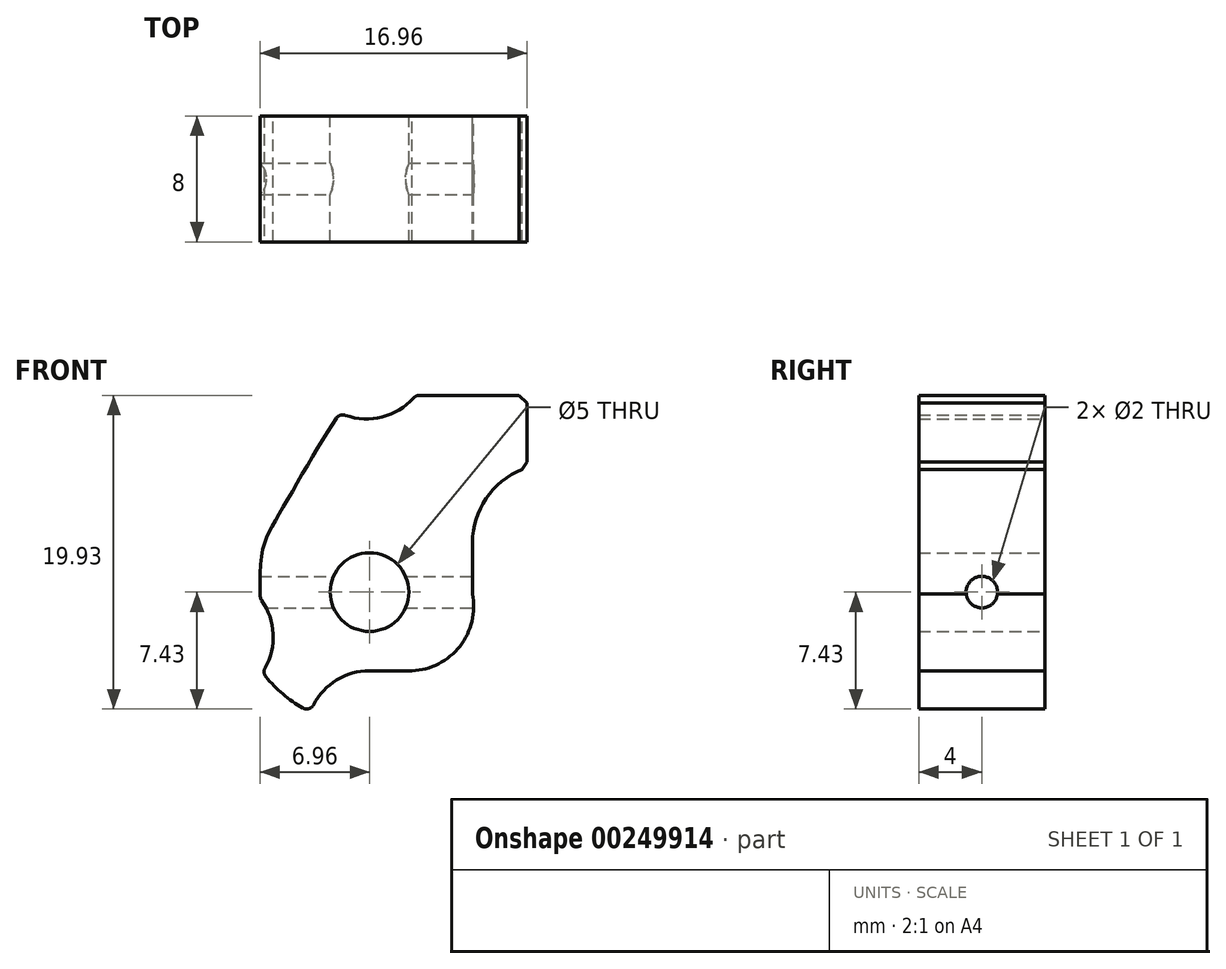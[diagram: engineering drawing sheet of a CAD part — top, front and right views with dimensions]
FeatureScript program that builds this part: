
annotation { "Feature Type Name" : "Feature", "Feature Type Description" : "" }
export const myFeature = defineFeature(function(context is Context, id is Id, definition is map)
    precondition{}
    {
        {
            var Q0;
            Q0=qCreatedBy(makeId("Front.planeOp"),FACE);
            var sketch = newSketch(context, id + "F0", { "sketchPlane" : qUnion([Q0])});
            skCircle(sketch, "E0", {"center": v(0, 0) * mm, "radius": 2.5 * mm});
            skLineSegment(sketch, "E1", {"start": v(0, -5) * mm, "end": v(2.7, -5) * mm});
            skArc(sketch, "E2", {"start": v(0, -5) * mm, "mid": v(-2.3, -5.72) * mm, "end": v(-3.76, -7.63) * mm});
            skArc(sketch, "E3", {"start": v(-6.8, -5.1) * mm, "mid": v(-6.12, -2.74) * mm, "end": v(-6.93, -0.43) * mm});
            skArc(sketch, "E4", {"start": v(-6.8, -5.1) * mm, "mid": v(-5.43, -6.54) * mm, "end": v(-3.76, -7.63) * mm});
            skLineSegment(sketch, "E5", {"start": v(6.54, -0.1) * mm, "end": v(6.54, 3.15) * mm});
            skArc(sketch, "E6.trimOffspring", {"start": v(2.7, -5) * mm, "mid": v(5.74, -3.44) * mm, "end": v(6.54, -0.1) * mm});
            skLineSegment(sketch, "E7", {"start": v(2.94, 12.5) * mm, "end": v(10, 12.5) * mm});
            skLineSegment(sketch, "E8", {"start": v(10, 12.5) * mm, "end": v(10, 7.9) * mm});
            skArc(sketch, "E9", {"start": v(10, 7.9) * mm, "mid": v(7.5, 6.09) * mm, "end": v(6.54, 3.15) * mm});
            skArc(sketch, "E10", {"start": v(-1.87, 11.37) * mm, "mid": v(0.73, 11.1) * mm, "end": v(2.94, 12.5) * mm});
            skPoint(sketch, "E11.orphan", {"position": v(0, 12.5) * mm});
            skPoint(sketch, "E12", {"position": v(-3.3, 12.5) * mm});
            skPoint(sketch, "E13.orphan", {"position": v(12.52, 15) * mm});
            skPoint(sketch, "E14.start.orphan", {"position": v(-12.88, 15) * mm});
            skFitSpline(sketch, "E15", {"points": [v(-6.93, -0.43) * mm, v(-5.77, 4.9) * mm, v(-1.87, 11.37) * mm], "startDerivative": vector(-1.05, 20.85) * mm, "endDerivative": vector(5.93, 8.17) * mm});
            skSolve(sketch);
        }
        {
            var Q0;
            Q0 = qSketchRegion(id + "F0", true);
            extrude(context, id + "F1", {"entities" : qUnion([Q0]), "depth" : 8 * mm});
        }
        {
            var Q0;
            Q0=makeQuery(id+"F1.opExtrude","SWEPT_EDGE",EDGE,{"disambiguationData":[OSD([sQuery(id+"F0.wireOp",EDGE,"E8"),sQuery(id+"F0.wireOp",EDGE,"E9")])]});
            var Q1;
            Q1=makeQuery(id+"F1.opExtrude","SWEPT_EDGE",EDGE,{"disambiguationData":[OSD([sQuery(id+"F0.wireOp",EDGE,"E7"),sQuery(id+"F0.wireOp",EDGE,"E8")])]});
            chamfer(context, id + "F2", {"entities" : qUnion([Q0, Q1]), "width" : .5 * mm, "tangentPropagation" : true});
        }
        {
            var Q0;
            Q0=makeQuery(id+"F1.opExtrude","SWEPT_EDGE",EDGE,{"disambiguationData":[OSD([sQuery(id+"F0.wireOp",EDGE,"E10"),sQuery(id+"F0.wireOp",EDGE,"E15")])]});
            var Q1;
            Q1=makeQuery(id+"F1.opExtrude","SWEPT_EDGE",EDGE,{"disambiguationData":[OSD([sQuery(id+"F0.wireOp",EDGE,"E7"),sQuery(id+"F0.wireOp",EDGE,"E10")])]});
            var Q2;
            Q2=makeQuery(id+"F1.opExtrude","SWEPT_EDGE",EDGE,{"disambiguationData":[OSD([sQuery(id+"F0.wireOp",EDGE,"E3"),sQuery(id+"F0.wireOp",EDGE,"E15")])]});
            var Q3;
            Q3=makeQuery(id+"F1.opExtrude","SWEPT_EDGE",EDGE,{"disambiguationData":[OSD([sQuery(id+"F0.wireOp",EDGE,"E3"),sQuery(id+"F0.wireOp",EDGE,"E4")])]});
            var Q4;
            Q4=makeQuery(id+"F1.opExtrude","SWEPT_EDGE",EDGE,{"disambiguationData":[OSD([sQuery(id+"F0.wireOp",EDGE,"E2"),sQuery(id+"F0.wireOp",EDGE,"E4")])]});
            fillet(context, id + "F3", {"entities" : qUnion([Q0, Q1, Q2, Q3, Q4]), "radius" : .5 * mm, "tangentPropagation" : true, "allowEdgeOverflow" : false});
        }
        {
            var Q0;
            Q0=qCreatedBy(makeId("Right.planeOp"),FACE);
            var sketch = newSketch(context, id + "F4", { "sketchPlane" : qUnion([Q0])});
            skCircle(sketch, "E16", {"center": v(-4, 0) * mm, "radius": 1 * mm});
            skSolve(sketch);
        }
        {
            var Q0;
            Q0 = qSketchRegion(id + "F4", true);
            extrude(context, id + "F5", {"entities" : qUnion([Q0]), "operationType" : NewBodyOperationType.REMOVE, "endBound" : BoundingType.SYMMETRIC, "oppositeDirection" : true, "depth" : 25 * mm});
        }
    });
